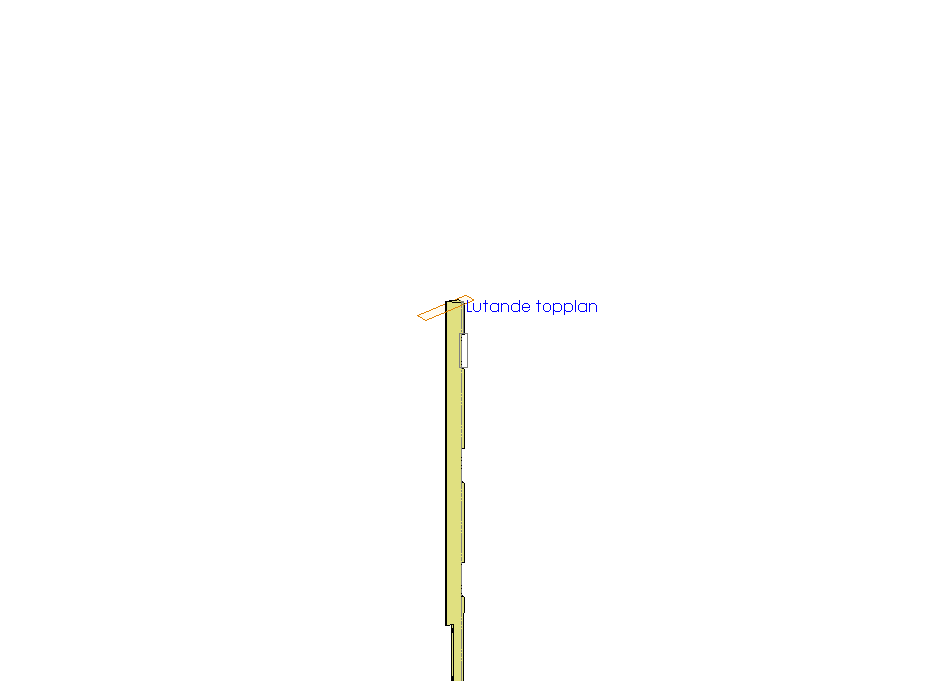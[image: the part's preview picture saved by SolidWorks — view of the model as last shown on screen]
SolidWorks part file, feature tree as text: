
SOLIDWORKS PART (.sldprt)
format: sldprt  version: not decoded by parser v0  size: 586,240 bytes
history: native  units: mm
features: sketch x10, cut_extrude x5, pattern_linear x3, plane x2, material x1, extrude x1, fillet x1 (+11 scaffold rows collapsed)
feature tree (34):
  scaffold x11  (default folders/planes/origin — collapsed)
  material  "Material <not specified>"
  sketch  "Layout tvärsnitt stolpe"  dims[c1.D3=~134.350288mm c1.D1=47.5mm c1.D2=45.0mm c2.D2=45.0deg]
  sketch  "Layout stolphöjd"  dims[D1=1100.0mm D2=50.0mm]
  sketch  "Sketch rombisk regel"  dims[D1=38.0mm D2=90.0mm D3=5.0mm]
  sketch  "Sketch rektangulär regel"  dims[D1=5.0mm D2=90.0mm D3=95.0mm D4=22.0mm]
  plane  "Lutande bottenplan"
  plane  "Lutande topplan"
  sketch  "Sketch2"  dims[c1.D3=~134.350288mm c1.D1=~55.710667mm c2.D1=45.0deg c2.D2=47.5mm]
  extrude  "Extrude höjd"  [1 undecoded]
  sketch  "Sketch5"
  cut_extrude  "Cut-rombisk regel"  [1 undecoded]
  pattern_linear  "LPattern rombisk regel"  Count1=5 Count2=1 Spacing1=180mm Spacing2=50mm
  sketch  "Sketch9"
  cut_extrude  "Cut-rektangulär regel"  [1 undecoded]
  pattern_linear  "LPattern rektangulär regel"  Count1=3 Count2=1 Spacing1=320mm Spacing2=50mm
  sketch  "Sketch6"  dims[c1.D2=5.0mm c1.D1=~56.950441mm c2.D2=~88.770247mm c2.D3=~88.770247mm c3.D2=~88.770247mm c3.D1=20.0mm c3.D3=45.0mm c4.D1=~19.682997mm c4.D4=~26.292349mm c5.D1=~26.292349mm c5.D4=~84.682997mm c6.D1=~84.682997mm c6.D4=~84.682997mm c7.D1=~84.682997mm c7.D4=~84.682997mm c8.D1=~84.682997mm c8.D4=~84.682997mm c9.D1=~84.682997mm c9.D4=~84.682997mm c10.D1=~84.682997mm c10.D3=45.0mm c11.D1=50.0mm]
  cut_extrude  "Cut-Skruvhål i höjdled"  [1 undecoded]
  pattern_linear  "LPattern skruvhål i höjdled"  Count1=3 Count2=1 Spacing1=360mm Spacing2=50mm
  sketch  "Sketch7"  dims[c1.D2=12.0mm c1.D3=12.0mm c1.D1=175.0mm c2.D3=135.0mm]
  cut_extrude  "Cut-Skruvhål för stolpfot"  [1 undecoded]
  sketch  "Sketch8"  dims[c1.D1=200.0mm c1.D2=~24.222046mm c2.D2=72.0deg c2.D3=22.0mm]
  cut_extrude  "Cut-Yta för stolpskobricka"  [1 undecoded]
  fillet  "Fillet1"  Radius=5mm
decode coverage: 12 of 20 modeling features carry decoded parameters
note: ~ marks probable driven/reference dimensions
note: 6 parameter values undecoded
summary: no parameter record found for 6 features
note: suppression state not decoded; provenance and decode notes live in map.json
